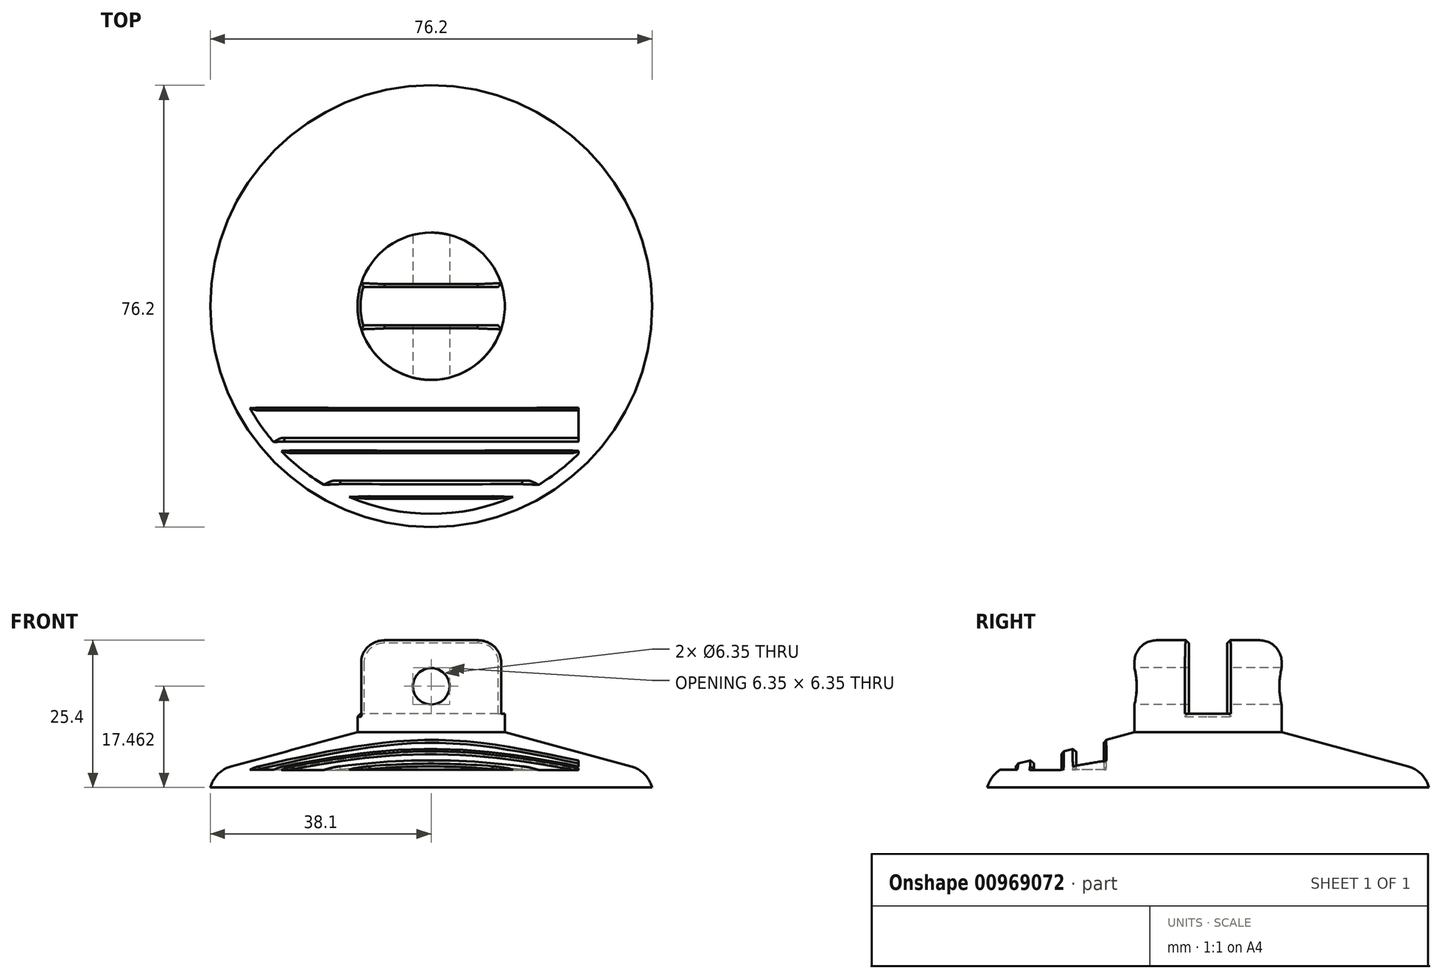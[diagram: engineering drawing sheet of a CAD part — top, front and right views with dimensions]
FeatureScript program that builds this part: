
annotation { "Feature Type Name" : "Feature", "Feature Type Description" : "" }
export const myFeature = defineFeature(function(context is Context, id is Id, definition is map)
    precondition{}
    {
        {
            var Q0;
            Q0=qCreatedBy(makeId("Front.planeOp"),FACE);
            var sketch = newSketch(context, id + "F0", { "sketchPlane" : qUnion([Q0])});
            skLineSegment(sketch, "E0", {"start": v(0, 0) * mm, "end": v(0, 25.4) * mm});
            skLineSegment(sketch, "E1", {"start": v(-37.01, 2.98) * mm, "end": v(-12.7, 9.52) * mm});
            skLineSegment(sketch, "E2", {"start": v(-12.7, 9.52) * mm, "end": v(-12.7, 25.4) * mm});
            skLineSegment(sketch, "E3", {"start": v(-12.7, 25.4) * mm, "end": v(0, 25.4) * mm});
            skLineSegment(sketch, "E4", {"start": v(-38.1, 0) * mm, "end": v(-37.01, 2.98) * mm});
            skLineSegment(sketch, "E5", {"start": v(-38.1, 0) * mm, "end": v(0, 0) * mm});
            skSolve(sketch);
        }
        {
            var Q0;
            Q0 = qSketchRegion(id + "F0", true);
            var Q1;
            Q1=sQuery(id+"F0.wireOp",EDGE,"E0");
            revolve(context, id + "F1", {"surfaceOperationType" : NewSurfaceOperationType.NEW, "entities" : qUnion([Q0]), "axis" : qUnion([Q1]), "revolveType" : RevolveType.FULL});
        }
        {
            var Q0;
            Q0=qCreatedBy(makeId("Right.planeOp"),FACE);
            var sketch = newSketch(context, id + "F2", { "sketchPlane" : qUnion([Q0])});
            skLineSegment(sketch, "E6.bottom", {"start": v(3.3, 44.29) * mm, "end": v(-3.3, 44.29) * mm});
            skLineSegment(sketch, "E6.top", {"start": v(3.3, 12.7) * mm, "end": v(-3.3, 12.7) * mm});
            skLineSegment(sketch, "E6.left", {"start": v(3.3, 44.29) * mm, "end": v(3.3, 12.7) * mm});
            skLineSegment(sketch, "E6.right", {"start": v(-3.3, 44.29) * mm, "end": v(-3.3, 12.7) * mm});
            skPoint(sketch, "E6.middle", {"position": v(0, 28.5) * mm});
            skSolve(sketch);
        }
        {
            var Q0;
            Q0 = qSketchRegion(id + "F2", true);
            extrude(context, id + "F3", {"entities" : qUnion([Q0]), "operationType" : NewBodyOperationType.REMOVE, "endBound" : BoundingType.THROUGH_ALL, "depth" : 25.4 * mm, "offsetDistance" : 25.4 * mm, "hasSecondDirection" : true, "secondDirectionOppositeDirection" : true, "secondDirectionDepth" : 25.4 * mm});
        }
        {
            var Q0;
            Q0=qCreatedBy(makeId("Front.planeOp"),FACE);
            var sketch = newSketch(context, id + "F4", { "sketchPlane" : qUnion([Q0])});
            skCircle(sketch, "E7", {"center": v(0, 17.46) * mm, "radius": 3.18 * mm});
            skSolve(sketch);
        }
        {
            var Q0;
            Q0 = qSketchRegion(id + "F4", true);
            extrude(context, id + "F5", {"entities" : qUnion([Q0]), "operationType" : NewBodyOperationType.REMOVE, "endBound" : BoundingType.THROUGH_ALL, "oppositeDirection" : true, "depth" : 25.4 * mm, "offsetDistance" : 25.4 * mm, "hasSecondDirection" : true, "secondDirectionOppositeDirection" : false, "secondDirectionDepth" : 25.4 * mm});
        }
        {
            var Q0;
            Q0=qCreatedBy(makeId("Right.planeOp"),FACE);
            var sketch = newSketch(context, id + "F6", { "sketchPlane" : qUnion([Q0])});
            skLineSegment(sketch, "E8.bottom", {"start": v(-33.16, 6.14) * mm, "end": v(-37.92, 6.14) * mm});
            skLineSegment(sketch, "E8.top", {"start": v(-33.16, 3.1) * mm, "end": v(-37.92, 3.1) * mm});
            skLineSegment(sketch, "E8.left", {"start": v(-33.16, 6.14) * mm, "end": v(-33.16, 3.1) * mm});
            skLineSegment(sketch, "E8.right", {"start": v(-37.92, 6.14) * mm, "end": v(-37.92, 3.1) * mm});
            skPoint(sketch, "E8.middle", {"position": v(-35.54, 4.62) * mm});
            skLineSegment(sketch, "E9.bottom", {"start": v(-25.29, 9.6) * mm, "end": v(-30.05, 9.6) * mm});
            skLineSegment(sketch, "E9.top", {"start": v(-25.29, 3) * mm, "end": v(-30.05, 3) * mm});
            skLineSegment(sketch, "E9.left", {"start": v(-25.29, 9.6) * mm, "end": v(-25.29, 3) * mm});
            skLineSegment(sketch, "E9.right", {"start": v(-30.05, 9.6) * mm, "end": v(-30.05, 3) * mm});
            skPoint(sketch, "E9.middle", {"position": v(-27.67, 6.3) * mm});
            skLineSegment(sketch, "E10.bottom", {"start": v(-17.95, 12.7) * mm, "end": v(-22.73, 12.7) * mm});
            skLineSegment(sketch, "E10.top", {"start": v(-17.95, 3.05) * mm, "end": v(-22.73, 3.05) * mm});
            skLineSegment(sketch, "E10.left", {"start": v(-17.95, 12.7) * mm, "end": v(-17.95, 3.05) * mm});
            skLineSegment(sketch, "E10.right", {"start": v(-22.73, 12.7) * mm, "end": v(-22.73, 3.05) * mm});
            skPoint(sketch, "E10.middle", {"position": v(-20.34, 7.87) * mm});
            skPoint(sketch, "E11.orphan", {"position": v(-43.4, 2.94) * mm});
            skSolve(sketch);
        }
        {
            var Q0;
            Q0 = qSketchRegion(id + "F6", true);
            extrude(context, id + "F7", {"entities" : qUnion([Q0]), "operationType" : NewBodyOperationType.REMOVE, "endBound" : BoundingType.THROUGH_ALL, "oppositeDirection" : true, "depth" : 25.4 * mm, "offsetDistance" : 25.4 * mm, "hasSecondDirection" : true, "secondDirectionOppositeDirection" : false, "secondDirectionDepth" : 25.4 * mm});
        }
        {
            var Q0;
            {var subQ0=sQuery(id+"F0.wireOp",EDGE,"E2");var subQ1=sQuery(id+"F0.wireOp",EDGE,"E3");Q0=makeQuery(id+"F3.boolean.opBoolean","SPLIT",EDGE,{"disambiguationData":[TD([makeQuery(id+"F3.opExtrude","SWEPT_FACE",FACE,{"disambiguationData":[OSD([sQuery(id+"F2.wireOp",EDGE,"E6.left")])]})])],"derivedFrom":makeQuery(id+"F1.opRevolve","SWEPT_EDGE",EDGE,{"disambiguationData":[OSD([subQ0,subQ1])]})});}
            var Q1;
            {var subQ0=sQuery(id+"F0.wireOp",EDGE,"E2");var subQ1=sQuery(id+"F0.wireOp",EDGE,"E3");Q1=makeQuery(id+"F3.boolean.opBoolean","SPLIT",EDGE,{"disambiguationData":[TD([makeQuery(id+"F3.opExtrude","SWEPT_FACE",FACE,{"disambiguationData":[OSD([sQuery(id+"F2.wireOp",EDGE,"E6.right")])]})])],"derivedFrom":makeQuery(id+"F1.opRevolve","SWEPT_EDGE",EDGE,{"disambiguationData":[OSD([subQ0,subQ1])]})});}
            fillet(context, id + "F8", {"entities" : qUnion([Q0, Q1]), "radius" : 3.8 * mm, "tangentPropagation" : true, "allowEdgeOverflow" : false});
        }
        {
            var Q0;
            Q0=makeQuery(id+"F1.opRevolve","SWEPT_EDGE",EDGE,{"disambiguationData":[OSD([sQuery(id+"F0.wireOp",EDGE,"E1"),sQuery(id+"F0.wireOp",EDGE,"E4")])]});
            fillet(context, id + "F9", {"entities" : qUnion([Q0]), "radius" : 5.08 * mm, "tangentPropagation" : true, "allowEdgeOverflow" : false});
        }
        {
            var Q0;
            Q0=makeQuery(id+"F3.boolean.opBoolean","INTERSECT",EDGE,{"disambiguationData":[OD(0.0)],"derivedFrom":[makeQuery(id+"F1.opRevolve","SWEPT_FACE",FACE,{"disambiguationData":[OSD([sQuery(id+"F0.wireOp",EDGE,"E2")])]}),makeQuery(id+"F3.opExtrude","SWEPT_FACE",FACE,{"disambiguationData":[OSD([sQuery(id+"F2.wireOp",EDGE,"E6.top")])]})]});
            var Q1;
            Q1=makeQuery(id+"F3.boolean.opBoolean","INTERSECT",EDGE,{"disambiguationData":[OD(0.0)],"derivedFrom":[makeQuery(id+"F1.opRevolve","SWEPT_FACE",FACE,{"disambiguationData":[OSD([sQuery(id+"F0.wireOp",EDGE,"E2")])]}),makeQuery(id+"F3.opExtrude","SWEPT_FACE",FACE,{"disambiguationData":[OSD([sQuery(id+"F2.wireOp",EDGE,"E6.left")])]})]});
            var Q2;
            Q2=makeQuery(id+"F3.boolean.opBoolean","INTERSECT",EDGE,{"disambiguationData":[OD(0.0)],"derivedFrom":[makeQuery(id+"F1.opRevolve","SWEPT_FACE",FACE,{"disambiguationData":[OSD([sQuery(id+"F0.wireOp",EDGE,"E2")])]}),makeQuery(id+"F3.opExtrude","SWEPT_FACE",FACE,{"disambiguationData":[OSD([sQuery(id+"F2.wireOp",EDGE,"E6.right")])]})]});
            var Q3;
            Q3=makeQuery(id+"Fc5F1cwUEbiQ1Cq_1.1.F7.boolean.opBoolean","INTERSECT",EDGE,{"derivedFrom":[makeQuery(id+"F1.opRevolve","SWEPT_FACE",FACE,{"disambiguationData":[OSD([sQuery(id+"F0.wireOp",EDGE,"E1")])]}),makeQuery(id+"Fc5F1cwUEbiQ1Cq_1.1.F7.opExtrude","SWEPT_FACE",FACE,{"disambiguationData":[OSD([sQuery(id+"F6.wireOp",EDGE,"E10.left")])]})]});
            var Q4;
            Q4=makeQuery(id+"Fc5F1cwUEbiQ1Cq_1.1.F7.boolean.opBoolean","INTERSECT",EDGE,{"derivedFrom":[makeQuery(id+"F1.opRevolve","SWEPT_FACE",FACE,{"disambiguationData":[OSD([sQuery(id+"F0.wireOp",EDGE,"E1")])]}),makeQuery(id+"Fc5F1cwUEbiQ1Cq_1.1.F7.opExtrude","SWEPT_FACE",FACE,{"disambiguationData":[OSD([sQuery(id+"F6.wireOp",EDGE,"E10.right")])]})]});
            var Q5;
            Q5=makeQuery(id+"Fc5F1cwUEbiQ1Cq_1.1.F7.boolean.opBoolean","INTERSECT",EDGE,{"derivedFrom":[makeQuery(id+"F1.opRevolve","SWEPT_FACE",FACE,{"disambiguationData":[OSD([sQuery(id+"F0.wireOp",EDGE,"E1")])]}),makeQuery(id+"Fc5F1cwUEbiQ1Cq_1.1.F7.opExtrude","SWEPT_FACE",FACE,{"disambiguationData":[OSD([sQuery(id+"F6.wireOp",EDGE,"E9.right")])]})]});
            var Q6;
            Q6=makeQuery(id+"Fc5F1cwUEbiQ1Cq_1.1.F7.boolean.opBoolean","INTERSECT",EDGE,{"derivedFrom":[makeQuery(id+"F1.opRevolve","SWEPT_FACE",FACE,{"disambiguationData":[OSD([sQuery(id+"F0.wireOp",EDGE,"E1")])]}),makeQuery(id+"Fc5F1cwUEbiQ1Cq_1.1.F7.opExtrude","SWEPT_FACE",FACE,{"disambiguationData":[OSD([sQuery(id+"F6.wireOp",EDGE,"E9.left")])]})]});
            var Q7;
            Q7=makeQuery(id+"Fc5F1cwUEbiQ1Cq_1.1.F7.boolean.opBoolean","INTERSECT",EDGE,{"derivedFrom":[makeQuery(id+"F1.opRevolve","SWEPT_FACE",FACE,{"disambiguationData":[OSD([sQuery(id+"F0.wireOp",EDGE,"E1")])]}),makeQuery(id+"Fc5F1cwUEbiQ1Cq_1.1.F7.opExtrude","SWEPT_FACE",FACE,{"disambiguationData":[OSD([sQuery(id+"F6.wireOp",EDGE,"E8.left")])]})]});
            var Q8;
            Q8=makeQuery(id+"Fc5F1cwUEbiQ1Cq_1.1.F7.boolean.opBoolean","INTERSECT",EDGE,{"derivedFrom":[makeQuery(id+"F1.opRevolve","SWEPT_FACE",FACE,{"disambiguationData":[OSD([sQuery(id+"F0.wireOp",EDGE,"E1")])]}),makeQuery(id+"Fc5F1cwUEbiQ1Cq_1.1.F7.opExtrude","SWEPT_FACE",FACE,{"disambiguationData":[OSD([sQuery(id+"F6.wireOp",EDGE,"E8.right")])]})]});
            var Q9;
            Q9=makeQuery(id+"F7.boolean.opBoolean","INTERSECT",EDGE,{"derivedFrom":[makeQuery(id+"F1.opRevolve","SWEPT_FACE",FACE,{"disambiguationData":[OSD([sQuery(id+"F0.wireOp",EDGE,"E1")])]}),makeQuery(id+"F7.opExtrude","SWEPT_FACE",FACE,{"disambiguationData":[OSD([sQuery(id+"F6.wireOp",EDGE,"E10.left")])]})]});
            var Q10;
            Q10=makeQuery(id+"F7.boolean.opBoolean","INTERSECT",EDGE,{"derivedFrom":[makeQuery(id+"F1.opRevolve","SWEPT_FACE",FACE,{"disambiguationData":[OSD([sQuery(id+"F0.wireOp",EDGE,"E1")])]}),makeQuery(id+"F7.opExtrude","SWEPT_FACE",FACE,{"disambiguationData":[OSD([sQuery(id+"F6.wireOp",EDGE,"E10.right")])]})]});
            var Q11;
            Q11=makeQuery(id+"F7.boolean.opBoolean","INTERSECT",EDGE,{"derivedFrom":[makeQuery(id+"F1.opRevolve","SWEPT_FACE",FACE,{"disambiguationData":[OSD([sQuery(id+"F0.wireOp",EDGE,"E1")])]}),makeQuery(id+"F7.opExtrude","SWEPT_FACE",FACE,{"disambiguationData":[OSD([sQuery(id+"F6.wireOp",EDGE,"E9.left")])]})]});
            var Q12;
            Q12=makeQuery(id+"F7.boolean.opBoolean","INTERSECT",EDGE,{"derivedFrom":[makeQuery(id+"F1.opRevolve","SWEPT_FACE",FACE,{"disambiguationData":[OSD([sQuery(id+"F0.wireOp",EDGE,"E1")])]}),makeQuery(id+"F7.opExtrude","SWEPT_FACE",FACE,{"disambiguationData":[OSD([sQuery(id+"F6.wireOp",EDGE,"E9.right")])]})]});
            var Q13;
            Q13=makeQuery(id+"F7.boolean.opBoolean","INTERSECT",EDGE,{"derivedFrom":[makeQuery(id+"F1.opRevolve","SWEPT_FACE",FACE,{"disambiguationData":[OSD([sQuery(id+"F0.wireOp",EDGE,"E1")])]}),makeQuery(id+"F7.opExtrude","SWEPT_FACE",FACE,{"disambiguationData":[OSD([sQuery(id+"F6.wireOp",EDGE,"E8.left")])]})]});
            var Q14;
            Q14=makeQuery(id+"F7.boolean.opBoolean","INTERSECT",EDGE,{"derivedFrom":[makeQuery(id+"F1.opRevolve","SWEPT_FACE",FACE,{"disambiguationData":[OSD([sQuery(id+"F0.wireOp",EDGE,"E1")])]}),makeQuery(id+"F7.opExtrude","SWEPT_FACE",FACE,{"disambiguationData":[OSD([sQuery(id+"F6.wireOp",EDGE,"E8.right")])]})]});
            chamfer(context, id + "F10", {"entities" : qUnion([Q0, Q1, Q2, Q3, Q4, Q5, Q6, Q7, Q8, Q9, Q10, Q11, Q12, Q13, Q14]), "width" : 0.5 * mm, "tangentPropagation" : true});
        }
    });
